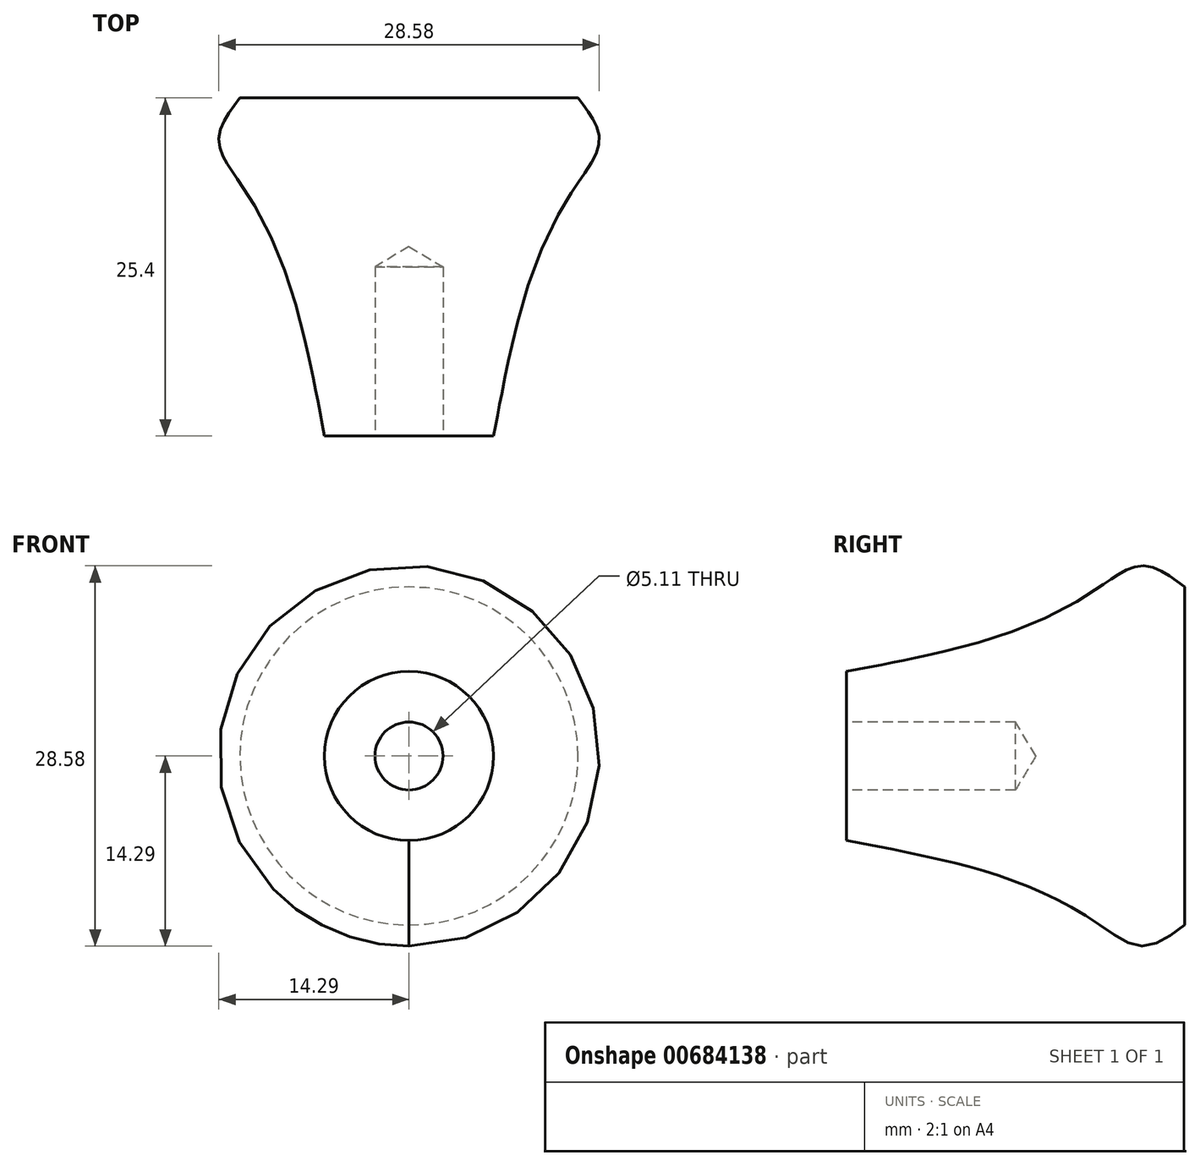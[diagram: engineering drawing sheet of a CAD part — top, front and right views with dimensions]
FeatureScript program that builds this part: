
annotation { "Feature Type Name" : "Feature", "Feature Type Description" : "" }
export const myFeature = defineFeature(function(context is Context, id is Id, definition is map)
    precondition{}
    {
        {
            var Q0;
            Q0=qCreatedBy(makeId("Front.planeOp"),FACE);
            var sketch = newSketch(context, id + "F0", { "sketchPlane" : qUnion([Q0])});
            skCircle(sketch, "E0", {"center": v(0, 0) * mm, "radius": 6.35 * mm});
            skSolve(sketch);
        }
        {
            var Q0;
            Q0=qCreatedBy(makeId("Front.planeOp"),FACE);
            cPlane(context, id + "F1", {"entities" : qUnion([Q0]), "cplaneType" : CPlaneType.OFFSET, "offset" : 6.35 * mm, "oppositeDirection" : true, "width" : 152.4 * mm, "height" : 152.4 * mm});
        }
        {
            var Q0;
            Q0=qCreatedBy(id+"F1.planeOp",FACE);
            var sketch = newSketch(context, id + "F2", { "sketchPlane" : qUnion([Q0])});
            skCircle(sketch, "E1", {"center": v(0, 0) * mm, "radius": 7.62 * mm});
            skSolve(sketch);
        }
        {
            var Q0;
            Q0=qCreatedBy(id+"F1.planeOp",FACE);
            cPlane(context, id + "F3", {"entities" : qUnion([Q0]), "cplaneType" : CPlaneType.OFFSET, "offset" : 12.7 * mm, "oppositeDirection" : true, "width" : 152.4 * mm, "height" : 152.4 * mm});
        }
        {
            var Q0;
            Q0=qCreatedBy(id+"F3.planeOp",FACE);
            var sketch = newSketch(context, id + "F4", { "sketchPlane" : qUnion([Q0])});
            skCircle(sketch, "E2", {"center": v(0, 0) * mm, "radius": 12.7 * mm});
            skSolve(sketch);
        }
        {
            var Q0;
            Q0=qCreatedBy(id+"F3.planeOp",FACE);
            cPlane(context, id + "F5", {"entities" : qUnion([Q0]), "cplaneType" : CPlaneType.OFFSET, "offset" : 3.17 * mm, "oppositeDirection" : true, "width" : 152.4 * mm, "height" : 152.4 * mm});
        }
        {
            var Q0;
            Q0=qCreatedBy(id+"F5.planeOp",FACE);
            var sketch = newSketch(context, id + "F6", { "sketchPlane" : qUnion([Q0])});
            skCircle(sketch, "E3", {"center": v(0, 0) * mm, "radius": 14.29 * mm});
            skSolve(sketch);
        }
        {
            var Q0;
            Q0=qCreatedBy(id+"F5.planeOp",FACE);
            cPlane(context, id + "F7", {"entities" : qUnion([Q0]), "cplaneType" : CPlaneType.OFFSET, "offset" : 3.17 * mm, "oppositeDirection" : true, "width" : 152.4 * mm, "height" : 152.4 * mm});
        }
        {
            var Q0;
            Q0=qCreatedBy(id+"F7.planeOp",FACE);
            var sketch = newSketch(context, id + "F8", { "sketchPlane" : qUnion([Q0])});
            skCircle(sketch, "E4.0", {"center": v(0, 0) * mm, "radius": 12.7 * mm});
            skSolve(sketch);
        }
        {
            var Q0;
            Q0=makeQuery(id+"F0.imprint","IMPRINT",FACE,{"disambiguationData":[TD([[makeQuery(id+"F0.imprint","IMPRINT",EDGE,{"derivedFrom":sQuery(id+"F0.wireOp",EDGE,"E0")}),1.0]])]});
            var Q1;
            Q1=makeQuery(id+"F2.imprint","IMPRINT",FACE,{"disambiguationData":[TD([[makeQuery(id+"F2.imprint","IMPRINT",EDGE,{"derivedFrom":sQuery(id+"F2.wireOp",EDGE,"E1")}),1.0]])]});
            var Q2;
            Q2=makeQuery(id+"F4.imprint","IMPRINT",FACE,{"disambiguationData":[TD([[makeQuery(id+"F4.imprint","IMPRINT",EDGE,{"derivedFrom":sQuery(id+"F4.wireOp",EDGE,"E2")}),1.0]])]});
            var Q3;
            Q3=makeQuery(id+"F6.imprint","IMPRINT",FACE,{"disambiguationData":[TD([[makeQuery(id+"F6.imprint","IMPRINT",EDGE,{"derivedFrom":sQuery(id+"F6.wireOp",EDGE,"E3")}),1.0]])]});
            var Q4;
            Q4 = qSketchRegion(id + "F8", true);
            loft(context, id + "F9", {"sheetProfilesArray" : [{ "sheetProfileEntities" : qUnion([Q0]) }, { "sheetProfileEntities" : qUnion([Q1]) }, { "sheetProfileEntities" : qUnion([Q2]) }, { "sheetProfileEntities" : qUnion([Q3]) }, { "sheetProfileEntities" : qUnion([Q4]) }]});
        }
        {
            var Q0;
            Q0=qCreatedBy(makeId("Front.planeOp"),FACE);
            var sketch = newSketch(context, id + "F10", { "sketchPlane" : qUnion([Q0])});
            skPoint(sketch, "E5", {"position": v(0, 0) * mm});
            skSolve(sketch);
        }
        {
            var Q0;
            Q0=sQuery(id+"F10.wireOp",VERTEX,"E5");
            var Q1;
            Q1=makeQuery(id+"F9.opLoft","SWEPT_BODY",BODY,{"disambiguationData":[OSD([makeQuery(id+"F0.imprint","IMPRINT",FACE,{"disambiguationData":[TD([[makeQuery(id+"F0.imprint","IMPRINT",EDGE,{"derivedFrom":sQuery(id+"F0.wireOp",EDGE,"E0")}),1.0]])]}),sQuery(id+"F2.wireOp",EDGE,"E1"),sQuery(id+"F4.wireOp",EDGE,"E2"),sQuery(id+"F6.wireOp",EDGE,"E3"),makeQuery(id+"F8.imprint","IMPRINT",FACE,{"disambiguationData":[TD([[makeQuery(id+"F8.imprint","IMPRINT",EDGE,{"derivedFrom":sQuery(id+"F8.wireOp",EDGE,"E4.0")}),1.0]])]})])]});
            hole(context, id + "F11", {"style" : HoleStyle.SIMPLE, "endStyle" : HoleEndStyle.BLIND, "standardTappedOrClearance" : lookupTablePath({ "standard" : "ANSI", "engagement" : "75%", "pitch" : "20 tpi", "size" : "1/4", "type" : "Tapped" }), "standardBlindInLast" : lookupTablePath({ "standard" : "ANSI", "engagement" : "75%", "pitch" : "20 tpi", "size" : "1/4", "type" : "Tapped" }), "holeDiameter" : 5.1 * mm, "majorDiameter" : 6.35 * mm, "showTappedDepth" : true, "holeDepth" : 12.7 * mm, "tappedDepth" : 8.9 * mm, "tapClearance" : 3, "locations" : qUnion([Q0]), "scope" : qUnion([Q1])});
        }
    });
